# Revit family: Eira Light Stor Lucka
name_source: partatom
category: Furniture
units: mm (PartAtom-declared; Revit-internal decimal feet)

## family parameters
Always vertical = Yes
Cut with Voids When Loaded = No
OmniClass Number = 23.40.20.00
OmniClass Title = General Furniture and Specialties
Room Calculation Point = No
Shared = No
Work Plane-Based = Yes

## types (1)
- Eira Light Stor Lucka
    CSI MasterFormat 2014 Code = 12 00 00
    CSI MasterFormat 2014 Title = Furnishings
    Default Elevation = 1219 mm
    Depth = 15 mm
    Description = Kapprumsinredning Eira Light stor lucka.
    Edition number = 1
    Height = 1140 mm
    IFC Classification = Furniture
    Keynote = Eira Light,
    Length = 250 mm
    Manufacturer = Form o miljö
    ManufacturerName = Form o miljö
    ManufacturerURL = https://formomiljo.se
    Model = Eira Light Stor Lucka
    OmniClass Code = 23-40 20 00
    OmniClass Description = General Furniture
    Primary Material = White Pigmented
    Product SKU = 608125
    Product group = Eira Light
    Product name = Eira Light Stor Lucka
    URL = https://www.sono.se
    Uniclass 2015 Code = EF_40_30
    Uniclass 2015 Name = Furnishings

## geometry (parser evidence)
native form markers: Sweep x3
no freeform markers — native parametric forms only
